# Revit family: PRD_FrankeWS_SoapDpnsrs_Heavy-DutySoapDispenser_SD300
name_source: partatom
category: Specialty Equipment
revit_build: Autodesk Revit 2018 (Build: 20190510_1515(x64)
units: mm (PartAtom-declared; Revit-internal decimal feet)

## family parameters
Cut with Voids When Loaded = No
Host = Face
OmniClass Number = 23.40.20.21.34
OmniClass Title = Soap Holders, Dispensers
Part Type = Normal
Room Calculation Point = No
Round Connector Dimension = Use Diameter
Shared = No

## types (1)
- SD300
    AssetType = Fixed
    BIMObjectName = PRD_AR_SoapDispensers_Heavy-DutySoapDispenser_SD300
    Category = Pr_40_70_22_81, Soap dispensers
    Color = Stainless steel
    Default Elevation = 1050 mm
    Description = Soap dispenser for wall mounting, stainless steel, surface satin finished, material thickness 14 gauge (2 mm), casing is held in place by a stainless steel rod fixed to the mounting plate and a security lock, suitable for liquid soaps and lotions, 1 liter soap tank, push button on front, incl. stainless steel screws and dowels.
    DurationUnit = year
    Features = stainless steel, surface satin finished, suitable for liquid soaps and lotions, 1 liter soap tank, push button on front.
    Finish = Satin finished
    Form = Wall mounted
    GrossWeight = 3.80 kg
    IfcExportAs = IfcFurnitureType
    IfcExportType = NOTDEFINED
    IntegralAccessories = Stainless steel screws and dowels incl.
    MainColor = Stainless steel
    Manufacturer = KWC Group AG
    ManufacturerName = KWC Group AG
    ManufacturerURL = www.kwc.com
    Material = Stainless steel
    MaterialsBody = Stainless steel
    MaterialsFinishAndColour = Stainless steel, satin finished
    Model = SD300
    ModelNumber = 2000057729
    ModelReference = SD300
    NBSDescription = Soap dispensers
    NBSReference = 45-35-72/358
    Name = HEAVY-DUTY soap dispenser SD300
    NetWeight = 3.50 kg
    NominalDepth = 127 mm
    NominalHeight = 320 mm  [stored 1.04987 ft]
    NominalLength = 128 mm  [stored 0.419948 ft]
    NominalWidth = 128 mm  [stored 0.419948 ft]
    Operation = Manual
    ProductInformation = https://pim.kwc.com
    Shape = Rectangular
    Size = 128 x 320 x 127 mm
    SoapDispenserMaterial = PRD_AR_StainlessSteel_SatinFinished
    Style = Soap dispenser
    TypeOfConsumable = Liquid soap
    TypeOfSoapContainer = Integrated refillable tank
    URL = www.kwc.com
    Uniclass2015Code = Pr_40_70_22_81
    Uniclass2015Title = Soap dispensers
    Uniclass2015Version = Products v1.5
    Version = 1
    WarrantyDurationUnit = year

note: [stored X ft] marks values corroborated as IEEE doubles in the binary element streams (Revit-internal decimal feet)

## geometry (parser evidence)
native form markers: Sweep x2
no freeform markers — native parametric forms only
